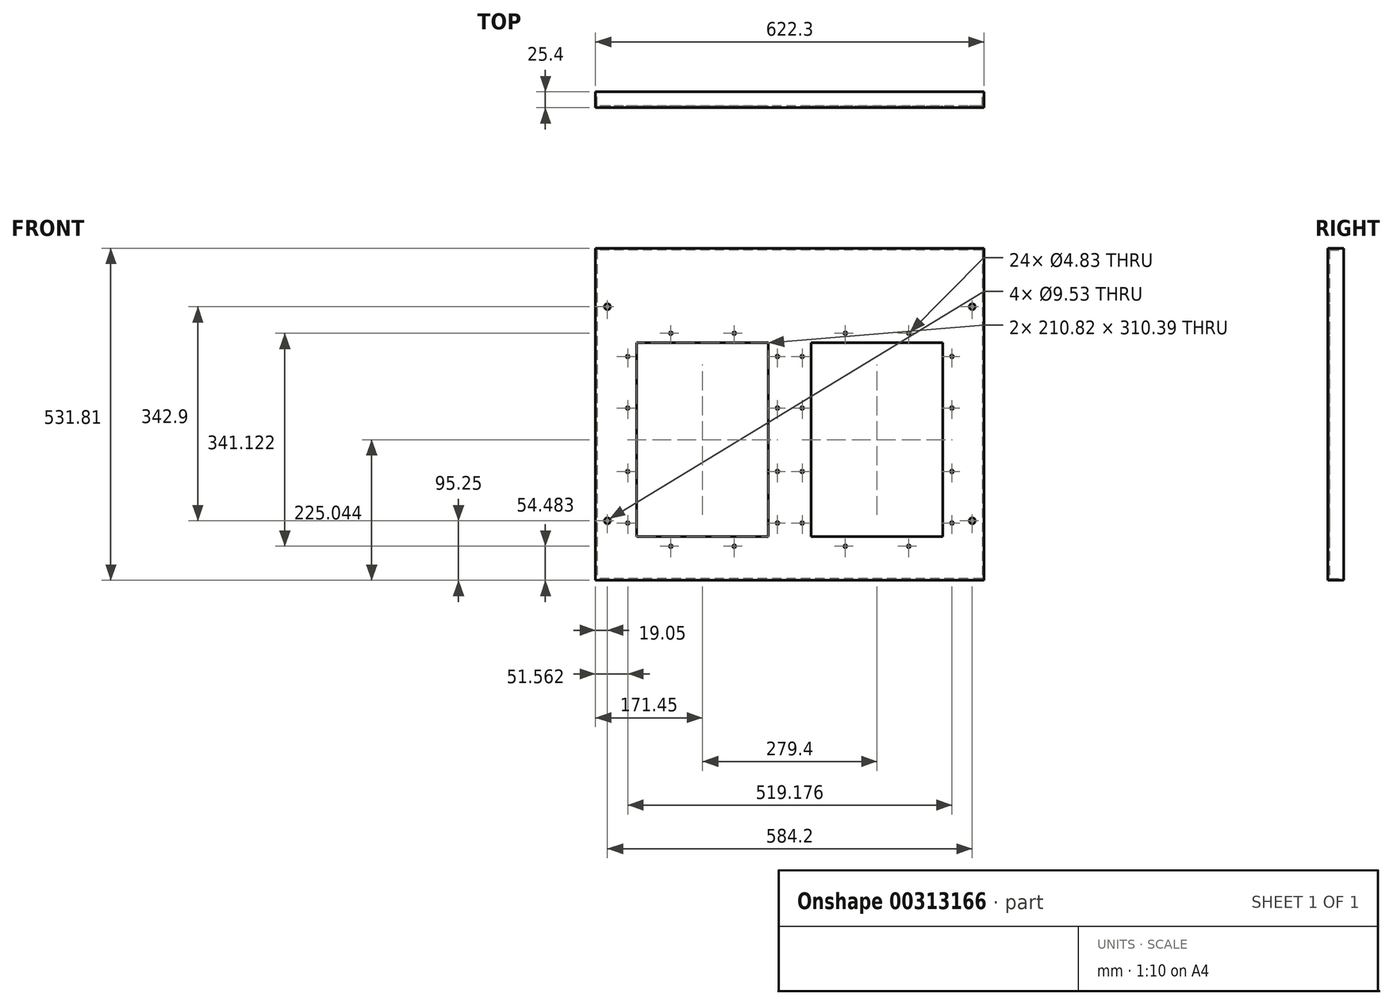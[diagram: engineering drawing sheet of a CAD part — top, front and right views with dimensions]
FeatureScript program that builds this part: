
annotation { "Feature Type Name" : "Feature", "Feature Type Description" : "" }
export const myFeature = defineFeature(function(context is Context, id is Id, definition is map)
    precondition{}
    {
        {
            var Q0;
            Q0=qCreatedBy(makeId("Front.planeOp"),FACE);
            var sketch = newSketch(context, id + "F0", { "sketchPlane" : qUnion([Q0])});
            skLineSegment(sketch, "E0.bottom", {"start": v(311.15, 531.81) * mm, "end": v(-311.15, 531.81) * mm});
            skLineSegment(sketch, "E0.top", {"start": v(311.15, 0) * mm, "end": v(-311.15, 0) * mm});
            skLineSegment(sketch, "E0.left", {"start": v(311.15, 531.81) * mm, "end": v(311.15, 0) * mm});
            skLineSegment(sketch, "E0.right", {"start": v(-311.15, 531.81) * mm, "end": v(-311.15, 0) * mm});
            skLineSegment(sketch, "E1.bottom", {"start": v(-34.29, 380.24) * mm, "end": v(-245.1, 380.24) * mm});
            skLineSegment(sketch, "E1.top", {"start": v(-34.29, 69.85) * mm, "end": v(-245.1, 69.85) * mm});
            skLineSegment(sketch, "E1.left", {"start": v(-34.29, 380.24) * mm, "end": v(-34.29, 69.85) * mm});
            skLineSegment(sketch, "E1.right", {"start": v(-245.1, 380.24) * mm, "end": v(-245.1, 69.85) * mm});
            skPoint(sketch, "E1.middle", {"position": v(-139.7, 225.04) * mm});
            skCircle(sketch, "E2", {"center": v(-190.5, 395.6) * mm, "radius": 2.41 * mm});
            skCircle(sketch, "E3", {"center": v(-88.9, 395.6) * mm, "radius": 2.41 * mm});
            skCircle(sketch, "E4", {"center": v(-19.81, 358.4) * mm, "radius": 2.41 * mm});
            skCircle(sketch, "E5", {"center": v(-19.81, 275.84) * mm, "radius": 2.41 * mm});
            skCircle(sketch, "E6", {"center": v(-19.81, 174.24) * mm, "radius": 2.41 * mm});
            skCircle(sketch, "E7", {"center": v(-19.81, 91.7) * mm, "radius": 2.41 * mm});
            skCircle(sketch, "E8", {"center": v(-190.5, 54.48) * mm, "radius": 2.41 * mm});
            skCircle(sketch, "E9", {"center": v(-88.9, 54.48) * mm, "radius": 2.41 * mm});
            skCircle(sketch, "E10", {"center": v(-259.59, 91.7) * mm, "radius": 2.41 * mm});
            skCircle(sketch, "E11", {"center": v(-259.59, 174.24) * mm, "radius": 2.41 * mm});
            skCircle(sketch, "E12", {"center": v(-259.59, 275.84) * mm, "radius": 2.41 * mm});
            skCircle(sketch, "E13", {"center": v(-259.59, 358.4) * mm, "radius": 2.41 * mm});
            skPoint(sketch, "E14.1.0.0", {"position": v(139.7, 225.04) * mm});
            skLineSegment(sketch, "E14.1.0.1", {"start": v(245.11, 380.24) * mm, "end": v(245.11, 69.85) * mm});
            skLineSegment(sketch, "E14.1.0.2", {"start": v(34.3, 380.24) * mm, "end": v(34.3, 69.85) * mm});
            skLineSegment(sketch, "E14.1.0.3", {"start": v(245.11, 69.85) * mm, "end": v(34.3, 69.85) * mm});
            skLineSegment(sketch, "E14.1.0.4", {"start": v(245.11, 380.24) * mm, "end": v(34.3, 380.24) * mm});
            skCircle(sketch, "E14.1.0.5", {"center": v(259.59, 91.7) * mm, "radius": 2.41 * mm});
            skCircle(sketch, "E14.1.0.6", {"center": v(19.81, 174.24) * mm, "radius": 2.41 * mm});
            skCircle(sketch, "E14.1.0.7", {"center": v(259.59, 275.84) * mm, "radius": 2.41 * mm});
            skCircle(sketch, "E14.1.0.8", {"center": v(88.9, 54.48) * mm, "radius": 2.41 * mm});
            skCircle(sketch, "E14.1.0.9", {"center": v(259.59, 358.4) * mm, "radius": 2.41 * mm});
            skCircle(sketch, "E14.1.0.10", {"center": v(190.5, 54.48) * mm, "radius": 2.41 * mm});
            skCircle(sketch, "E14.1.0.11", {"center": v(88.9, 395.6) * mm, "radius": 2.41 * mm});
            skCircle(sketch, "E14.1.0.12", {"center": v(190.5, 395.6) * mm, "radius": 2.41 * mm});
            skCircle(sketch, "E14.1.0.13", {"center": v(259.59, 174.24) * mm, "radius": 2.41 * mm});
            skCircle(sketch, "E14.1.0.14", {"center": v(19.81, 358.4) * mm, "radius": 2.41 * mm});
            skCircle(sketch, "E14.1.0.15", {"center": v(19.81, 275.84) * mm, "radius": 2.41 * mm});
            skCircle(sketch, "E14.1.0.16", {"center": v(19.81, 91.7) * mm, "radius": 2.41 * mm});
            skLineSegment(sketch, "E14.direction1", {"start": v(-245.1, 69.85) * mm, "end": v(34.3, 69.85) * mm, "construction": true});
            skCircle(sketch, "E15", {"center": v(292.1, 95.25) * mm, "radius": 4.76 * mm});
            skCircle(sketch, "E16", {"center": v(292.1, 438.15) * mm, "radius": 4.76 * mm});
            skCircle(sketch, "E17", {"center": v(-292.1, 438.15) * mm, "radius": 4.76 * mm});
            skCircle(sketch, "E18", {"center": v(-292.1, 95.25) * mm, "radius": 4.76 * mm});
            skSolve(sketch);
        }
        {
            var Q0;
            Q0=qSketchRegion(id+"F0",true);
            extrude(context, id + "F1", {"entities" : qUnion([Q0]), "depth" : 25.4 * mm});
        }
        {
            var Q0;
            Q0=makeQuery(id+"F1.opExtrude","CAP_FACE",FACE,{"disambiguationData":[OSD([sQuery(id+"F0.wireOp",EDGE,"E0.bottom"),sQuery(id+"F0.wireOp",EDGE,"E0.top"),sQuery(id+"F0.wireOp",EDGE,"E0.left"),sQuery(id+"F0.wireOp",EDGE,"E0.right"),sQuery(id+"F0.wireOp",EDGE,"E1.bottom"),sQuery(id+"F0.wireOp",EDGE,"E1.top"),sQuery(id+"F0.wireOp",EDGE,"E1.left"),sQuery(id+"F0.wireOp",EDGE,"E1.right"),sQuery(id+"F0.wireOp",EDGE,"E2"),sQuery(id+"F0.wireOp",EDGE,"E3"),sQuery(id+"F0.wireOp",EDGE,"E4"),sQuery(id+"F0.wireOp",EDGE,"E5"),sQuery(id+"F0.wireOp",EDGE,"E6"),sQuery(id+"F0.wireOp",EDGE,"E7"),sQuery(id+"F0.wireOp",EDGE,"E8"),sQuery(id+"F0.wireOp",EDGE,"E9"),sQuery(id+"F0.wireOp",EDGE,"E10"),sQuery(id+"F0.wireOp",EDGE,"E11"),sQuery(id+"F0.wireOp",EDGE,"E12"),sQuery(id+"F0.wireOp",EDGE,"E13"),sQuery(id+"F0.wireOp",EDGE,"E14.1.0.1"),sQuery(id+"F0.wireOp",EDGE,"E14.1.0.2"),sQuery(id+"F0.wireOp",EDGE,"E14.1.0.3"),sQuery(id+"F0.wireOp",EDGE,"E14.1.0.4"),sQuery(id+"F0.wireOp",EDGE,"E14.1.0.5"),sQuery(id+"F0.wireOp",EDGE,"E14.1.0.6"),sQuery(id+"F0.wireOp",EDGE,"E14.1.0.7"),sQuery(id+"F0.wireOp",EDGE,"E14.1.0.8"),sQuery(id+"F0.wireOp",EDGE,"E14.1.0.9"),sQuery(id+"F0.wireOp",EDGE,"E14.1.0.10"),sQuery(id+"F0.wireOp",EDGE,"E14.1.0.11"),sQuery(id+"F0.wireOp",EDGE,"E14.1.0.12"),sQuery(id+"F0.wireOp",EDGE,"E14.1.0.13"),sQuery(id+"F0.wireOp",EDGE,"E14.1.0.14"),sQuery(id+"F0.wireOp",EDGE,"E14.1.0.15"),sQuery(id+"F0.wireOp",EDGE,"E14.1.0.16")])],"isStart":true});
            shell(context, id + "F2", {"entities" : qUnion([Q0]), "thickness" : 2.54 * mm});
        }
        {
            var Q0;
            Q0=makeQuery(id+"F2.opShell","OFFSET_FACE",FACE,{"disambiguationData":[OSD([sQuery(id+"F0.wireOp",EDGE,"E0.bottom")])]});
            var sketch = newSketch(context, id + "F3", { "sketchPlane" : qUnion([Q0])});
            skLineSegment(sketch, "E19.bottom", {"start": v(-308.6, 22.86) * mm, "end": v(308.61, 22.86) * mm});
            skLineSegment(sketch, "E19.top", {"start": v(-308.6, 0) * mm, "end": v(308.61, 0) * mm});
            skLineSegment(sketch, "E19.left", {"start": v(-308.6, 22.86) * mm, "end": v(-308.6, 0) * mm});
            skLineSegment(sketch, "E19.right", {"start": v(308.61, 22.86) * mm, "end": v(308.61, 0) * mm});
            skSolve(sketch);
        }
        {
            var Q0;
            Q0=qSketchRegion(id+"F3",true);
            var Q1;
            Q1=makeQuery(id+"F2.opShell","OFFSET_FACE",FACE,{"disambiguationData":[OSD([sQuery(id+"F0.wireOp",EDGE,"E0.top")])]});
            extrude(context, id + "F4", {"entities" : qUnion([Q0]), "operationType" : NewBodyOperationType.REMOVE, "endBound" : BoundingType.UP_TO_SURFACE, "endBoundEntityFace" : qUnion([Q1]), "depth" : 25.4 * mm});
        }
    });
